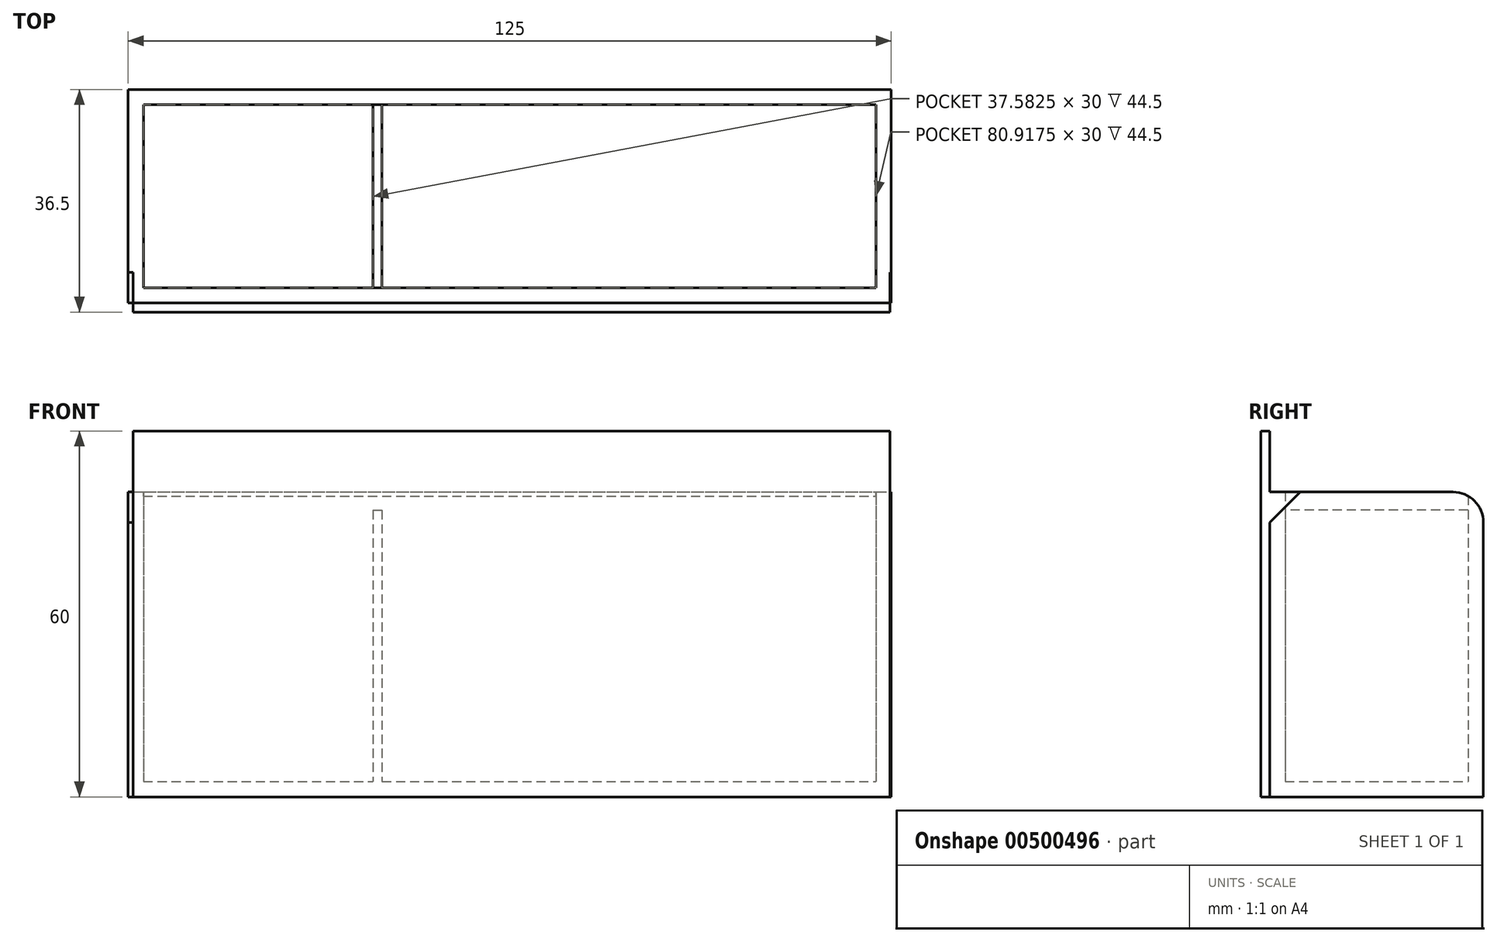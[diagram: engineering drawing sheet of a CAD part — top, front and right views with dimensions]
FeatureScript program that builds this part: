
annotation { "Feature Type Name" : "Feature", "Feature Type Description" : "" }
export const myFeature = defineFeature(function(context is Context, id is Id, definition is map)
    precondition{}
    {
        {
            var Q0;
            Q0=qCreatedBy(makeId("Top.planeOp"),FACE);
            var sketch = newSketch(context, id + "F0", { "sketchPlane" : qUnion([Q0])});
            skLineSegment(sketch, "E0.bottom", {"start": v(-64.99, 17.7) * mm, "end": v(60.01, 17.7) * mm});
            skLineSegment(sketch, "E0.top", {"start": v(-64.99, -17.3) * mm, "end": v(60.01, -17.3) * mm});
            skLineSegment(sketch, "E0.left", {"start": v(-64.99, 17.7) * mm, "end": v(-64.99, -17.3) * mm});
            skLineSegment(sketch, "E0.right", {"start": v(60.01, 17.7) * mm, "end": v(60.01, -17.3) * mm});
            skSolve(sketch);
        }
        {
            var Q0;
            Q0 = qSketchRegion(id + "F0", true);
            extrude(context, id + "F1", {"entities" : qUnion([Q0]), "depth" : 50 * mm});
        }
        {
            var Q0;
            Q0=makeQuery(id+"F1.opExtrude","CAP_FACE",FACE,{"disambiguationData":[OSD([sQuery(id+"F0.wireOp",EDGE,"E0.bottom"),sQuery(id+"F0.wireOp",EDGE,"E0.top"),sQuery(id+"F0.wireOp",EDGE,"E0.left"),sQuery(id+"F0.wireOp",EDGE,"E0.right")])],"isStart":false});
            shell(context, id + "F2", {"entities" : qUnion([Q0]), "thickness" : 2.5 * mm});
        }
        {
            var Q0;
            Q0=makeQuery(id+"F1.opExtrude","CAP_EDGE",EDGE,{"disambiguationData":[OSD([sQuery(id+"F0.wireOp",EDGE,"E0.bottom")])],"isStart":false});
            fillet(context, id + "F3", {"entities" : qUnion([Q0]), "radius" : 5 * mm, "tangentPropagation" : true, "allowEdgeOverflow" : false});
        }
        {
            var Q0;
            Q0=qCreatedBy(makeId("Top.planeOp"),FACE);
            var sketch = newSketch(context, id + "F4", { "sketchPlane" : qUnion([Q0])});
            skLineSegment(sketch, "E1", {"start": v(-24.9, 15.22) * mm, "end": v(-24.9, -14.92) * mm});
            skLineSegment(sketch, "E2", {"start": v(-23.4, 15.23) * mm, "end": v(-23.4, -14.9) * mm});
            skLineSegment(sketch, "E3", {"start": v(-23.4, -14.9) * mm, "end": v(-24.9, -14.92) * mm});
            skLineSegment(sketch, "E4", {"start": v(-23.4, 15.23) * mm, "end": v(-24.9, 15.22) * mm});
            skLineSegment(sketch, "E5", {"start": v(-24.9, 15.22) * mm, "end": v(-23.4, 15.23) * mm});
            skSolve(sketch);
        }
        {
            var Q0;
            Q0 = qSketchRegion(id + "F4", true);
            extrude(context, id + "F5", {"entities" : qUnion([Q0]), "operationType" : NewBodyOperationType.ADD, "depth" : 47 * mm});
        }
        {
            var Q0;
            Q0=qCreatedBy(makeId("Top.planeOp"),FACE);
            var sketch = newSketch(context, id + "F6", { "sketchPlane" : qUnion([Q0])});
            skLineSegment(sketch, "E6.bottom", {"start": v(59.8, -17.3) * mm, "end": v(-64.18, -17.3) * mm});
            skLineSegment(sketch, "E6.top", {"start": v(59.8, -18.8) * mm, "end": v(-64.18, -18.8) * mm});
            skLineSegment(sketch, "E6.left", {"start": v(59.8, -17.3) * mm, "end": v(59.8, -18.8) * mm});
            skLineSegment(sketch, "E6.right", {"start": v(-64.18, -17.3) * mm, "end": v(-64.18, -18.8) * mm});
            skSolve(sketch);
        }
        {
            var Q0;
            Q0 = qSketchRegion(id + "F6", true);
            extrude(context, id + "F7", {"entities" : qUnion([Q0]), "operationType" : NewBodyOperationType.ADD, "depth" : 60 * mm});
        }
        {
            var Q0;
            {var subQ0=sQuery(id+"F0.wireOp",EDGE,"E0.top");Q0=makeQuery(id+"F7.boolean.opBoolean","SPLIT",EDGE,{"disambiguationData":[topologyDisambiguationEdgeConnected([makeQuery(id+"F1.opExtrude","CAP_FACE",FACE,{"disambiguationData":[OSD([sQuery(id+"F0.wireOp",EDGE,"E0.bottom"),subQ0,sQuery(id+"F0.wireOp",EDGE,"E0.left"),sQuery(id+"F0.wireOp",EDGE,"E0.right")])],"isStart":false}),makeQuery(id+"F7.opExtrude","SWEPT_FACE",FACE,{"disambiguationData":[OSD([sQuery(id+"F6.wireOp",EDGE,"E6.bottom")])]})])],"derivedFrom":makeQuery(id+"F1.opExtrude","CAP_EDGE",EDGE,{"disambiguationData":[OSD([subQ0])],"isStart":false})});}
            chamfer(context, id + "F8", {"entities" : qUnion([Q0]), "width" : 5 * mm, "tangentPropagation" : true});
        }
    });
